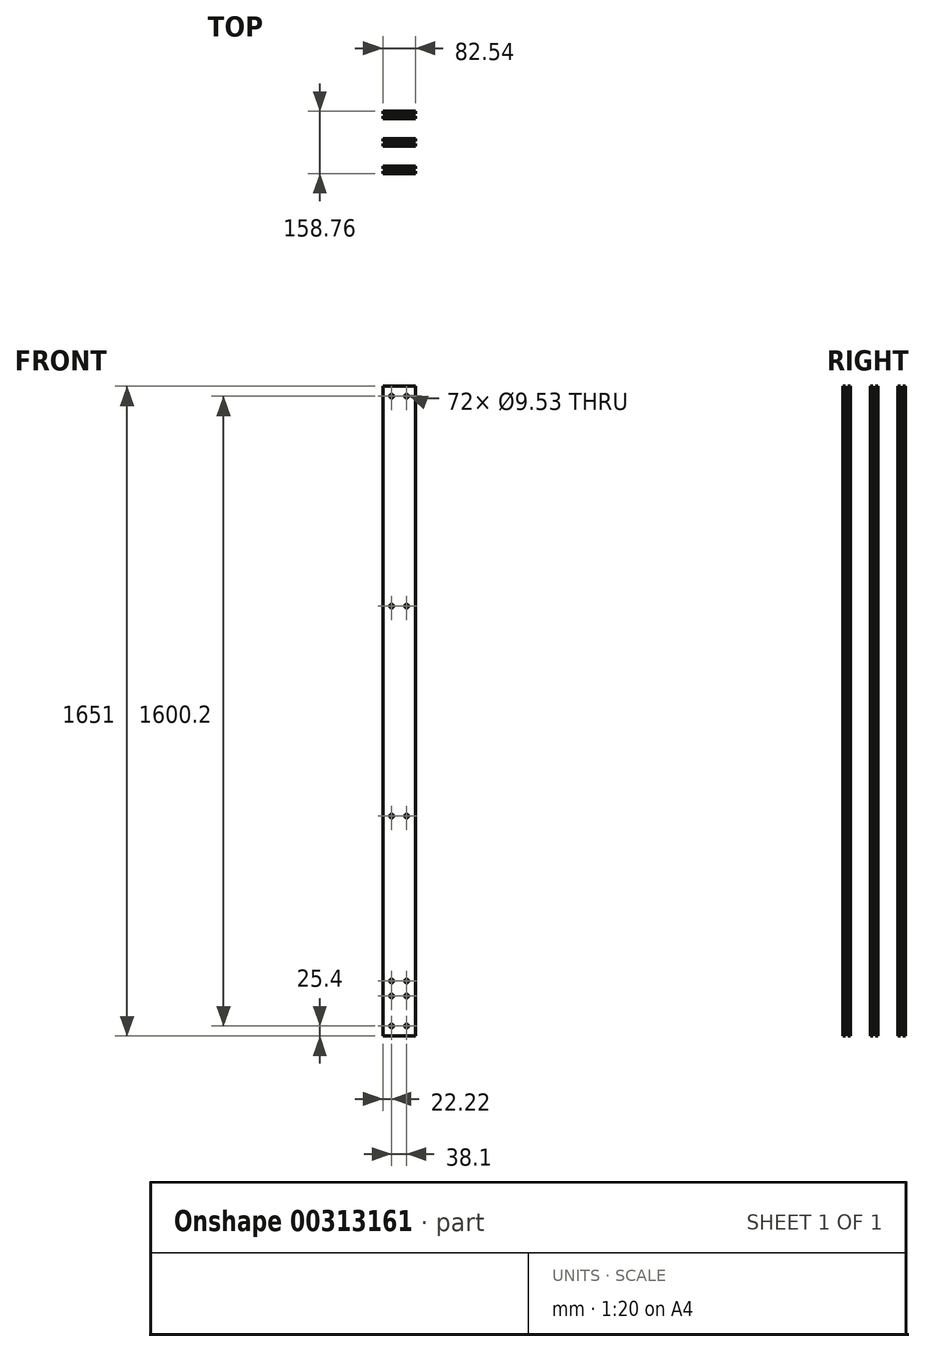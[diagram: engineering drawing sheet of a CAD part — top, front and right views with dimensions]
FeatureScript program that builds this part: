
annotation { "Feature Type Name" : "Feature", "Feature Type Description" : "" }
export const myFeature = defineFeature(function(context is Context, id is Id, definition is map)
    precondition{}
    {
        {
            var Q0;
            Q0=qCreatedBy(makeId("Top.planeOp"),FACE);
            var sketch = newSketch(context, id + "F0", { "sketchPlane" : qUnion([Q0])});
            skLineSegment(sketch, "E0.bottom", {"start": v(41.28, 3.18) * mm, "end": v(-41.28, 3.18) * mm});
            skLineSegment(sketch, "E0.top", {"start": v(41.28, -3.18) * mm, "end": v(-41.28, -3.18) * mm});
            skLineSegment(sketch, "E0.left", {"start": v(41.28, 3.17) * mm, "end": v(41.28, -3.18) * mm});
            skLineSegment(sketch, "E0.right", {"start": v(-41.28, 3.17) * mm, "end": v(-41.28, -3.18) * mm});
            skPoint(sketch, "E0.middle", {"position": v(0, 0) * mm});
            skLineSegment(sketch, "E1.bottom", {"start": v(41.28, 9.53) * mm, "end": v(-41.28, 9.53) * mm});
            skLineSegment(sketch, "E1.top", {"start": v(41.28, 15.88) * mm, "end": v(-41.28, 15.88) * mm});
            skLineSegment(sketch, "E1.left", {"start": v(41.28, 9.53) * mm, "end": v(41.28, 15.88) * mm});
            skLineSegment(sketch, "E1.right", {"start": v(-41.28, 9.53) * mm, "end": v(-41.28, 15.88) * mm});
            skPoint(sketch, "E1.middle", {"position": v(0, 12.7) * mm});
            skPoint(sketch, "E2.0.1.0", {"position": v(0, 82.55) * mm});
            skLineSegment(sketch, "E2.0.1.1", {"start": v(41.28, 85.73) * mm, "end": v(-41.28, 85.73) * mm});
            skLineSegment(sketch, "E2.0.1.2", {"start": v(41.28, 79.38) * mm, "end": v(-41.28, 79.38) * mm});
            skLineSegment(sketch, "E2.0.1.3", {"start": v(-41.28, 73.03) * mm, "end": v(-41.28, 66.68) * mm});
            skLineSegment(sketch, "E2.0.1.4", {"start": v(41.28, 73.03) * mm, "end": v(41.28, 66.68) * mm});
            skLineSegment(sketch, "E2.0.1.5", {"start": v(41.28, 66.68) * mm, "end": v(-41.28, 66.68) * mm});
            skLineSegment(sketch, "E2.0.1.6", {"start": v(41.28, 73.03) * mm, "end": v(-41.28, 73.03) * mm});
            skPoint(sketch, "E2.0.1.7", {"position": v(0, 69.85) * mm});
            skLineSegment(sketch, "E2.0.1.8", {"start": v(41.28, 79.38) * mm, "end": v(41.28, 85.73) * mm});
            skLineSegment(sketch, "E2.0.1.9", {"start": v(-41.28, 79.38) * mm, "end": v(-41.28, 85.73) * mm});
            skPoint(sketch, "E2.0.2.0", {"position": v(0, 152.4) * mm});
            skLineSegment(sketch, "E2.0.2.1", {"start": v(41.28, 155.58) * mm, "end": v(-41.28, 155.58) * mm});
            skLineSegment(sketch, "E2.0.2.2", {"start": v(41.28, 149.23) * mm, "end": v(-41.28, 149.23) * mm});
            skLineSegment(sketch, "E2.0.2.3", {"start": v(-41.28, 142.88) * mm, "end": v(-41.28, 136.53) * mm});
            skLineSegment(sketch, "E2.0.2.4", {"start": v(41.28, 142.88) * mm, "end": v(41.28, 136.53) * mm});
            skLineSegment(sketch, "E2.0.2.5", {"start": v(41.28, 136.53) * mm, "end": v(-41.28, 136.53) * mm});
            skLineSegment(sketch, "E2.0.2.6", {"start": v(41.28, 142.88) * mm, "end": v(-41.28, 142.88) * mm});
            skPoint(sketch, "E2.0.2.7", {"position": v(0, 139.7) * mm});
            skLineSegment(sketch, "E2.0.2.8", {"start": v(41.28, 149.23) * mm, "end": v(41.28, 155.58) * mm});
            skLineSegment(sketch, "E2.0.2.9", {"start": v(-41.28, 149.23) * mm, "end": v(-41.28, 155.58) * mm});
            skLineSegment(sketch, "E2.direction1", {"start": v(-41.28, -3.18) * mm, "end": v(-12.7, -3.18) * mm, "construction": true});
            skLineSegment(sketch, "E2.direction2", {"start": v(-41.28, -3.17) * mm, "end": v(-41.28, 66.68) * mm, "construction": true});
            skSolve(sketch);
        }
        {
            var Q0;
            Q0 = qSketchRegion(id + "F0", true);
            extrude(context, id + "F1", {"entities" : qUnion([Q0]), "endBound" : BoundingType.SYMMETRIC, "depth" : 1651 * mm});
        }
        {
            var Q0;
            Q0=makeQuery(id+"F1.opExtrude","SWEPT_FACE",FACE,{"disambiguationData":[OSD([sQuery(id+"F0.wireOp",EDGE,"E0.top")])]});
            var sketch = newSketch(context, id + "F2", { "sketchPlane" : qUnion([Q0])});
            skCircle(sketch, "E3", {"center": v(-19.05, -723.9) * mm, "radius": 4.76 * mm});
            skCircle(sketch, "E4", {"center": v(-19.05, -685.8) * mm, "radius": 4.76 * mm});
            skCircle(sketch, "E5", {"center": v(19.05, -685.8) * mm, "radius": 4.76 * mm});
            skCircle(sketch, "E6", {"center": v(19.05, -723.9) * mm, "radius": 4.76 * mm});
            skCircle(sketch, "E7", {"center": v(19.05, -800.1) * mm, "radius": 4.76 * mm});
            skCircle(sketch, "E8", {"center": v(-19.05, -800.1) * mm, "radius": 4.76 * mm});
            skCircle(sketch, "E9.0.1.0", {"center": v(19.05, -266.7) * mm, "radius": 4.76 * mm});
            skCircle(sketch, "E9.0.1.1", {"center": v(-19.05, -266.7) * mm, "radius": 4.76 * mm});
            skCircle(sketch, "E9.0.2.0", {"center": v(19.05, 266.7) * mm, "radius": 4.76 * mm});
            skCircle(sketch, "E9.0.2.1", {"center": v(-19.05, 266.7) * mm, "radius": 4.76 * mm});
            skCircle(sketch, "E9.0.3.0", {"center": v(19.05, 800.1) * mm, "radius": 4.76 * mm});
            skCircle(sketch, "E9.0.3.1", {"center": v(-19.05, 800.1) * mm, "radius": 4.76 * mm});
            skLineSegment(sketch, "E9.direction1", {"start": v(-19.05, -800.1) * mm, "end": v(6.35, -800.1) * mm, "construction": true});
            skLineSegment(sketch, "E9.direction2", {"start": v(-19.05, -800.1) * mm, "end": v(-19.05, -266.7) * mm, "construction": true});
            skSolve(sketch);
        }
        {
            var Q0;
            Q0 = qSketchRegion(id + "F2", true);
            extrude(context, id + "F3", {"entities" : qUnion([Q0]), "operationType" : NewBodyOperationType.REMOVE, "endBound" : BoundingType.THROUGH_ALL, "oppositeDirection" : true, "depth" : 25.4 * mm});
        }
    });
